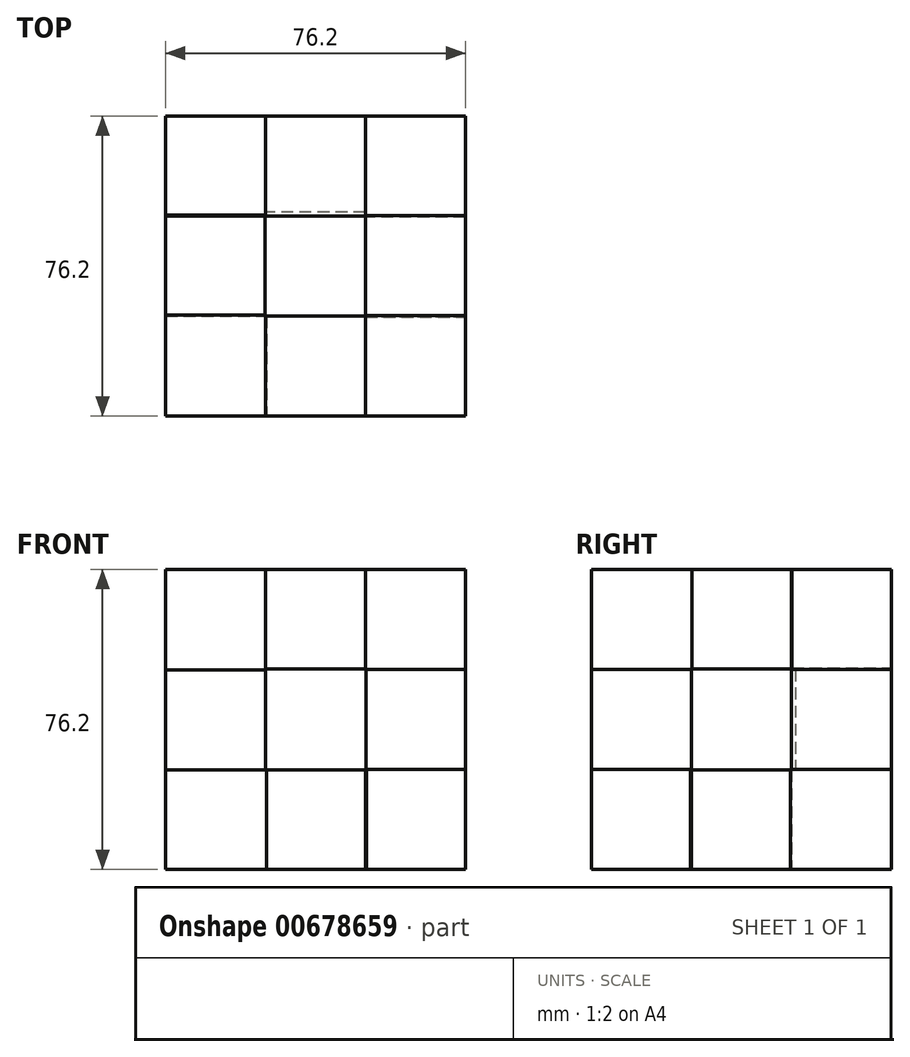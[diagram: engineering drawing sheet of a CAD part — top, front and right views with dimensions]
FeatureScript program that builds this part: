
annotation { "Feature Type Name" : "Feature", "Feature Type Description" : "" }
export const myFeature = defineFeature(function(context is Context, id is Id, definition is map)
    precondition{}
    {
        {
            var Q0;
            Q0=qCreatedBy(makeId("Front.planeOp"),FACE);
            var sketch = newSketch(context, id + "F0", { "sketchPlane" : qUnion([Q0])});
            skLineSegment(sketch, "E0.bottom", {"start": v(-38.1, 38.1) * mm, "end": v(38.1, 38.1) * mm});
            skLineSegment(sketch, "E0.top", {"start": v(-38.1, -38.1) * mm, "end": v(38.1, -38.1) * mm});
            skLineSegment(sketch, "E0.left", {"start": v(-38.1, 38.1) * mm, "end": v(-38.1, -38.1) * mm});
            skLineSegment(sketch, "E0.right", {"start": v(38.1, 38.1) * mm, "end": v(38.1, -38.1) * mm});
            skPoint(sketch, "E0.middle", {"position": v(0, 0) * mm});
            skSolve(sketch);
        }
        {
            var Q0;
            Q0=makeQuery(id+"F0.imprint","IMPRINT",FACE,{"disambiguationData":[TD([[makeQuery(id+"F0.imprint","IMPRINT",EDGE,{"derivedFrom":sQuery(id+"F0.wireOp",EDGE,"E0.bottom")}),-1.0]])]});
            extrude(context, id + "F1", {"entities" : qUnion([Q0]), "depth" : 76.2 * mm, "offsetDistance" : 25.4 * mm});
        }
        {
            var Q0;
            Q0=qCreatedBy(makeId("Front.planeOp"),FACE);
            var sketch = newSketch(context, id + "F2", { "sketchPlane" : qUnion([Q0])});
            skLineSegment(sketch, "E1.bottom", {"start": v(12.7, 12.7) * mm, "end": v(-12.7, 12.7) * mm});
            skLineSegment(sketch, "E1.top", {"start": v(12.7, -12.7) * mm, "end": v(-12.7, -12.7) * mm});
            skLineSegment(sketch, "E1.left", {"start": v(12.7, 12.7) * mm, "end": v(12.7, -12.7) * mm});
            skLineSegment(sketch, "E1.right", {"start": v(-12.7, 12.7) * mm, "end": v(-12.7, -12.7) * mm});
            skPoint(sketch, "E1.middle", {"position": v(0, 0) * mm});
            skSolve(sketch);
        }
        {
            var Q0;
            Q0=qCreatedBy(makeId("Front.planeOp"),FACE);
            var sketch = newSketch(context, id + "F3", { "sketchPlane" : qUnion([Q0])});
            skLineSegment(sketch, "E2.bottom", {"start": v(-12.75, -12.67) * mm, "end": v(-38.15, -12.67) * mm});
            skLineSegment(sketch, "E2.top", {"start": v(-12.75, 12.73) * mm, "end": v(-38.15, 12.73) * mm});
            skLineSegment(sketch, "E2.left", {"start": v(-12.75, -12.67) * mm, "end": v(-12.75, 12.73) * mm});
            skLineSegment(sketch, "E2.right", {"start": v(-38.15, -12.67) * mm, "end": v(-38.15, 12.73) * mm});
            skSolve(sketch);
        }
        {
            var Q0;
            Q0=qCreatedBy(makeId("Front.planeOp"),FACE);
            var sketch = newSketch(context, id + "F4", { "sketchPlane" : qUnion([Q0])});
            skLineSegment(sketch, "E3.bottom", {"start": v(-12.67, 13.13) * mm, "end": v(12.73, 13.13) * mm});
            skLineSegment(sketch, "E3.top", {"start": v(-12.67, 38.53) * mm, "end": v(12.73, 38.53) * mm});
            skLineSegment(sketch, "E3.left", {"start": v(-12.67, 13.13) * mm, "end": v(-12.67, 38.53) * mm});
            skLineSegment(sketch, "E3.right", {"start": v(12.73, 13.13) * mm, "end": v(12.73, 38.53) * mm});
            skSolve(sketch);
        }
        {
            var Q0;
            Q0=qCreatedBy(makeId("Front.planeOp"),FACE);
            var sketch = newSketch(context, id + "F5", { "sketchPlane" : qUnion([Q0])});
            skLineSegment(sketch, "E4.bottom", {"start": v(12.77, 12.7) * mm, "end": v(38.17, 12.7) * mm});
            skLineSegment(sketch, "E4.top", {"start": v(12.77, -12.7) * mm, "end": v(38.17, -12.7) * mm});
            skLineSegment(sketch, "E4.left", {"start": v(12.77, 12.7) * mm, "end": v(12.77, -12.7) * mm});
            skLineSegment(sketch, "E4.right", {"start": v(38.17, 12.7) * mm, "end": v(38.17, -12.7) * mm});
            skSolve(sketch);
        }
        {
            var Q0;
            Q0=qCreatedBy(makeId("Front.planeOp"),FACE);
            var sketch = newSketch(context, id + "F6", { "sketchPlane" : qUnion([Q0])});
            skLineSegment(sketch, "E5.bottom", {"start": v(12.72, -12.85) * mm, "end": v(-12.68, -12.85) * mm});
            skLineSegment(sketch, "E5.top", {"start": v(12.72, -38.25) * mm, "end": v(-12.68, -38.25) * mm});
            skLineSegment(sketch, "E5.left", {"start": v(12.72, -12.85) * mm, "end": v(12.72, -38.25) * mm});
            skLineSegment(sketch, "E5.right", {"start": v(-12.68, -12.85) * mm, "end": v(-12.68, -38.25) * mm});
            skSolve(sketch);
        }
        {
            var Q0;
            Q0 = qSketchRegion(id + "F3", true);
            var Q1;
            Q1 = qSketchRegion(id + "F4", true);
            var Q2;
            Q2 = qSketchRegion(id + "F5", true);
            var Q3;
            Q3 = qSketchRegion(id + "F6", true);
            extrude(context, id + "F7", {"entities" : qUnion([Q0, Q1, Q2, Q3]), "operationType" : NewBodyOperationType.REMOVE, "depth" : 25.4 * mm, "offsetDistance" : 25.4 * mm});
        }
        {
            var Q0;
            Q0=qCreatedBy(makeId("Right.planeOp"),FACE);
            cPlane(context, id + "F8", {"entities" : qUnion([Q0]), "cplaneType" : CPlaneType.OFFSET, "offset" : 38.1 * mm, "width" : 152.4 * mm, "height" : 152.4 * mm});
        }
        {
            var Q0;
            Q0=qCreatedBy(makeId("Front.planeOp"),FACE);
            cPlane(context, id + "F9", {"entities" : qUnion([Q0]), "cplaneType" : CPlaneType.OFFSET, "offset" : 38.1 * mm, "width" : 152.4 * mm, "height" : 152.4 * mm});
        }
        {
            var Q0;
            Q0=qCreatedBy(id+"F9.planeOp",FACE);
            cPlane(context, id + "F10", {"entities" : qUnion([Q0]), "cplaneType" : CPlaneType.OFFSET, "offset" : 38.1 * mm, "width" : 152.4 * mm, "height" : 152.4 * mm});
        }
        {
            var Q0;
            Q0=qCreatedBy(id+"F10.planeOp",FACE);
            var sketch = newSketch(context, id + "F11", { "sketchPlane" : qUnion([Q0])});
            skLineSegment(sketch, "E6.bottom", {"start": v(-12.67, 12.89) * mm, "end": v(12.73, 12.89) * mm});
            skLineSegment(sketch, "E6.top", {"start": v(-12.67, 38.29) * mm, "end": v(12.73, 38.29) * mm});
            skLineSegment(sketch, "E6.left", {"start": v(-12.67, 12.89) * mm, "end": v(-12.67, 38.29) * mm});
            skLineSegment(sketch, "E6.right", {"start": v(12.73, 12.89) * mm, "end": v(12.73, 38.29) * mm});
            skSolve(sketch);
        }
        {
            var Q0;
            Q0=qCreatedBy(id+"F10.planeOp",FACE);
            var sketch = newSketch(context, id + "F12", { "sketchPlane" : qUnion([Q0])});
            skLineSegment(sketch, "E7.bottom", {"start": v(12.82, -12.7) * mm, "end": v(38.22, -12.7) * mm});
            skLineSegment(sketch, "E7.top", {"start": v(12.82, 12.7) * mm, "end": v(38.22, 12.7) * mm});
            skLineSegment(sketch, "E7.left", {"start": v(12.82, -12.7) * mm, "end": v(12.82, 12.7) * mm});
            skLineSegment(sketch, "E7.right", {"start": v(38.22, -12.7) * mm, "end": v(38.22, 12.7) * mm});
            skSolve(sketch);
        }
        {
            var Q0;
            Q0=qCreatedBy(id+"F10.planeOp",FACE);
            var sketch = newSketch(context, id + "F13", { "sketchPlane" : qUnion([Q0])});
            skLineSegment(sketch, "E8.bottom", {"start": v(-12.48, -38.19) * mm, "end": v(12.92, -38.19) * mm});
            skLineSegment(sketch, "E8.top", {"start": v(-12.48, -12.79) * mm, "end": v(12.92, -12.79) * mm});
            skLineSegment(sketch, "E8.left", {"start": v(-12.48, -38.19) * mm, "end": v(-12.48, -12.79) * mm});
            skLineSegment(sketch, "E8.right", {"start": v(12.92, -38.19) * mm, "end": v(12.92, -12.79) * mm});
            skSolve(sketch);
        }
        {
            var Q0;
            Q0=qCreatedBy(id+"F10.planeOp",FACE);
            var sketch = newSketch(context, id + "F14", { "sketchPlane" : qUnion([Q0])});
            skLineSegment(sketch, "E9.bottom", {"start": v(-38.13, -12.77) * mm, "end": v(-12.73, -12.77) * mm});
            skLineSegment(sketch, "E9.top", {"start": v(-38.13, 12.63) * mm, "end": v(-12.73, 12.63) * mm});
            skLineSegment(sketch, "E9.left", {"start": v(-38.13, -12.77) * mm, "end": v(-38.13, 12.63) * mm});
            skLineSegment(sketch, "E9.right", {"start": v(-12.73, -12.77) * mm, "end": v(-12.73, 12.63) * mm});
            skSolve(sketch);
        }
        {
            var Q0;
            Q0 = qSketchRegion(id + "F14", true);
            var Q1;
            Q1 = qSketchRegion(id + "F13", true);
            var Q2;
            Q2 = qSketchRegion(id + "F12", true);
            var Q3;
            Q3 = qSketchRegion(id + "F11", true);
            extrude(context, id + "F15", {"entities" : qUnion([Q0, Q1, Q2, Q3]), "operationType" : NewBodyOperationType.REMOVE, "oppositeDirection" : true, "depth" : 25.4 * mm, "offsetDistance" : 25.4 * mm});
        }
        {
            var Q0;
            Q0=qCreatedBy(id+"F8.planeOp",FACE);
            var sketch = newSketch(context, id + "F16", { "sketchPlane" : qUnion([Q0])});
            skLineSegment(sketch, "E10.bottom", {"start": v(-50.67, 12.86) * mm, "end": v(-25.27, 12.86) * mm});
            skLineSegment(sketch, "E10.top", {"start": v(-50.67, 38.26) * mm, "end": v(-25.27, 38.26) * mm});
            skLineSegment(sketch, "E10.left", {"start": v(-50.67, 12.86) * mm, "end": v(-50.67, 38.26) * mm});
            skLineSegment(sketch, "E10.right", {"start": v(-25.27, 12.86) * mm, "end": v(-25.27, 38.26) * mm});
            skSolve(sketch);
        }
        {
            var Q0;
            Q0=qCreatedBy(id+"F8.planeOp",FACE);
            var sketch = newSketch(context, id + "F17", { "sketchPlane" : qUnion([Q0])});
            skLineSegment(sketch, "E11.bottom", {"start": v(-51.06, -38.17) * mm, "end": v(-25.66, -38.17) * mm});
            skLineSegment(sketch, "E11.top", {"start": v(-51.06, -12.77) * mm, "end": v(-25.66, -12.77) * mm});
            skLineSegment(sketch, "E11.left", {"start": v(-51.06, -38.17) * mm, "end": v(-51.06, -12.77) * mm});
            skLineSegment(sketch, "E11.right", {"start": v(-25.66, -38.17) * mm, "end": v(-25.66, -12.77) * mm});
            skSolve(sketch);
        }
        {
            var Q0;
            Q0 = qSketchRegion(id + "F16", true);
            var Q1;
            Q1 = qSketchRegion(id + "F17", true);
            extrude(context, id + "F18", {"entities" : qUnion([Q0, Q1]), "operationType" : NewBodyOperationType.REMOVE, "oppositeDirection" : true, "depth" : 25.4 * mm, "offsetDistance" : 25.4 * mm});
        }
        {
            var Q0;
            Q0=qCreatedBy(makeId("Top.planeOp"),FACE);
            cPlane(context, id + "F19", {"entities" : qUnion([Q0]), "cplaneType" : CPlaneType.OFFSET, "offset" : 38.1 * mm, "width" : 152.4 * mm, "height" : 152.4 * mm});
        }
        {
            var Q0;
            Q0=qCreatedBy(id+"F19.planeOp",FACE);
            var sketch = newSketch(context, id + "F20", { "sketchPlane" : qUnion([Q0])});
            skLineSegment(sketch, "E12.bottom", {"start": v(-38.25, -50.6) * mm, "end": v(-12.85, -50.6) * mm});
            skLineSegment(sketch, "E12.top", {"start": v(-38.25, -25.2) * mm, "end": v(-12.85, -25.2) * mm});
            skLineSegment(sketch, "E12.left", {"start": v(-38.25, -50.6) * mm, "end": v(-38.25, -25.2) * mm});
            skLineSegment(sketch, "E12.right", {"start": v(-12.85, -50.6) * mm, "end": v(-12.85, -25.2) * mm});
            skSolve(sketch);
        }
        {
            var Q0;
            Q0 = qSketchRegion(id + "F20", true);
            extrude(context, id + "F21", {"entities" : qUnion([Q0]), "operationType" : NewBodyOperationType.REMOVE, "oppositeDirection" : true, "depth" : 25.4 * mm, "offsetDistance" : 25.4 * mm});
        }
        {
            var Q0;
            Q0=makeQuery(id+"F2.imprint","IMPRINT",FACE,{"disambiguationData":[TD([[makeQuery(id+"F2.imprint","IMPRINT",EDGE,{"derivedFrom":sQuery(id+"F2.wireOp",EDGE,"E1.bottom")}),1.0]])]});
            extrude(context, id + "F22", {"entities" : qUnion([Q0]), "operationType" : NewBodyOperationType.REMOVE, "depth" : 24.38 * mm, "offsetDistance" : 25.4 * mm});
        }
    });
